# Revit family: AFX-Sienna-LED_Sconce-1
name_source: partatom
category: Lighting Fixtures
units: mm (PartAtom-declared; Revit-internal decimal feet)

## family parameters
Cut with Voids When Loaded = No
Host = Face
Light Source = Yes
Part Type = Normal
Room Calculation Point = No
Round Connector Dimension = Use Diameter
Shared = No

## types (1)
- SIES0414L30D1BK
    Apparent Load = 0 VA
    Assembly Code = D5020200
    Canopy Finish = AFX - Black Steel
    Color Filter = 16777215
    Colour Rendering Index = 90
    Default Elevation = 48"
    Depth = 2"
    Description = LED Sconce - 4 3/4"W x 2"D x 13 1/2"H
    Diffuser Finish = AFX - White Acrylic
    Dimming Lamp Color Temperature Shift = <None>
    Emit Shape Visible in Rendering = No
    Emit from Rectangle Length = 48"
    Emit from Rectangle Width = 24"
    Frame Finish = AFX - Black Steel
    Height = 13 1/2"
    Keynote = 12500
    Lamp = LED
    Manufacturer = AFX Inc
    Model = SIES0414L30D1BK
    Photometric Web File = SIES0414L30D1XX LR37496-W1.IES
    Power Factor = 1
    Product Documentation Link = https://www.afxinc.com
    Tilt Angle = -90.00°
    Type Comments = Sienna
    URL = https://www.afxinc.com
    Voltage = 120 V
    Wattage Comments = 10
    Width = 4 3/4"

## geometry (parser evidence)
native form markers: Sweep x2
no freeform markers — native parametric forms only
